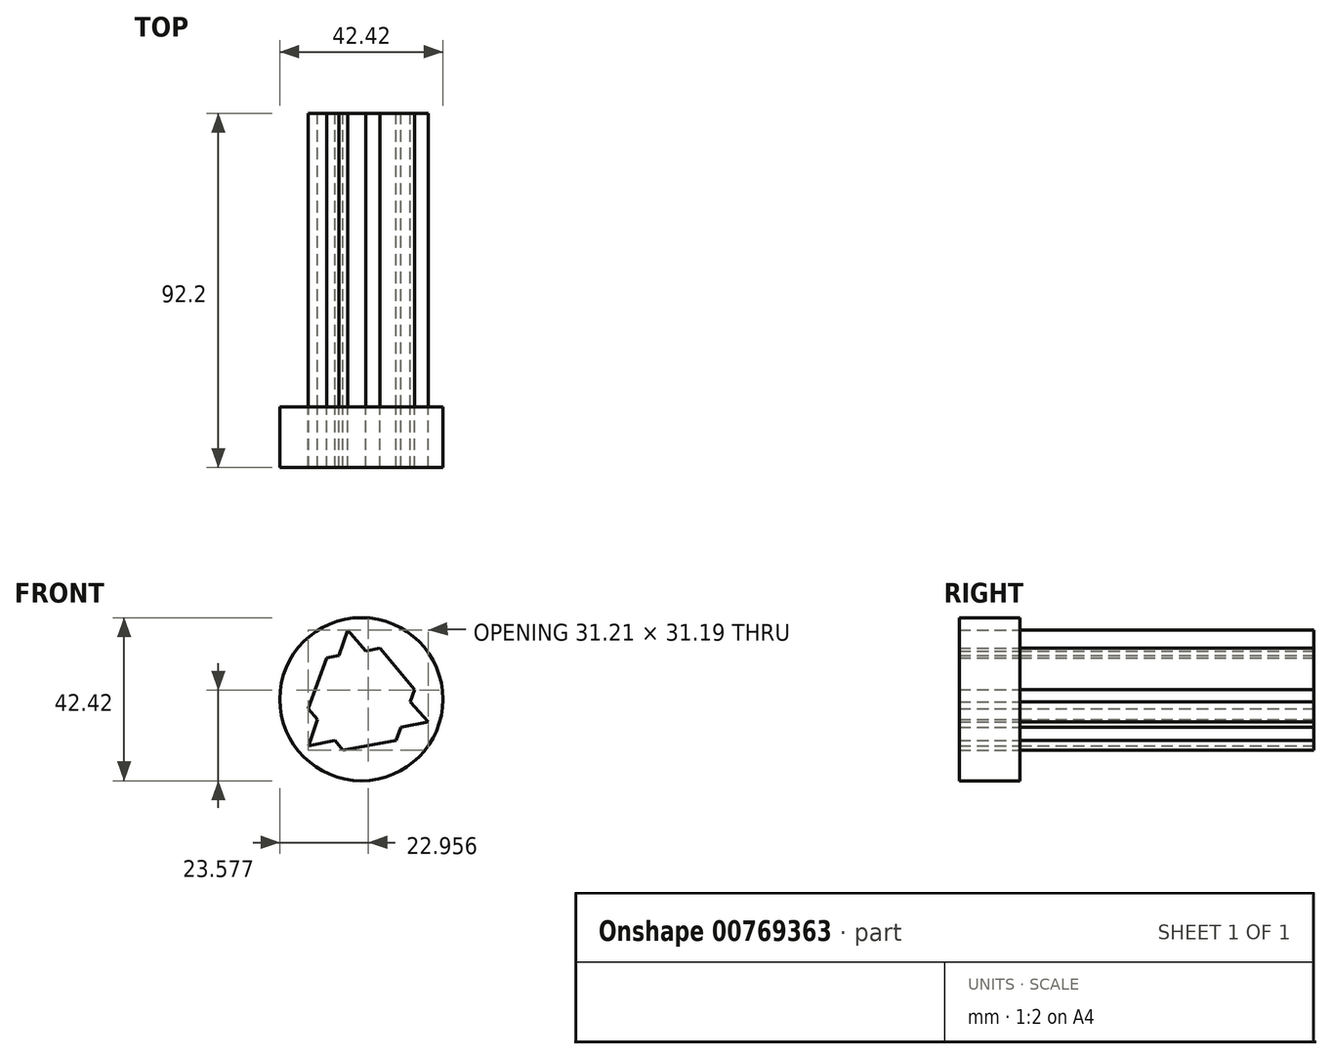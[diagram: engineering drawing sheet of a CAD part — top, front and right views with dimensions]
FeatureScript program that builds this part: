
annotation { "Feature Type Name" : "Feature", "Feature Type Description" : "" }
export const myFeature = defineFeature(function(context is Context, id is Id, definition is map)
    precondition{}
    {
        {
            var Q0;
            Q0=qCreatedBy(makeId("Front.planeOp"),FACE);
            var sketch = newSketch(context, id + "F0", { "sketchPlane" : qUnion([Q0])});
            skCircle(sketch, "E0.cCircle", {"center": v(0, 0) * mm, "radius": 14.08 * mm, "construction": true});
            skLineSegment(sketch, "E0.0", {"start": v(-9.05, 10.78) * mm, "end": v(4.8, 13.23) * mm});
            skLineSegment(sketch, "E0.1", {"start": v(4.8, 13.23) * mm, "end": v(13.86, 2.45) * mm});
            skLineSegment(sketch, "E0.2", {"start": v(13.86, 2.45) * mm, "end": v(9.05, -10.78) * mm});
            skLineSegment(sketch, "E0.3", {"start": v(9.05, -10.78) * mm, "end": v(-4.8, -13.23) * mm});
            skLineSegment(sketch, "E0.4", {"start": v(-4.8, -13.23) * mm, "end": v(-13.86, -2.45) * mm});
            skLineSegment(sketch, "E0.5", {"start": v(-13.86, -2.45) * mm, "end": v(-9.05, 10.78) * mm});
            skCircle(sketch, "E1.cCircle", {"center": v(0, 0) * mm, "radius": 18.32 * mm, "construction": true});
            skLineSegment(sketch, "E1.0", {"start": v(-3.6, 17.96) * mm, "end": v(17.35, -5.87) * mm});
            skLineSegment(sketch, "E1.1", {"start": v(17.35, -5.87) * mm, "end": v(-13.76, -12.1) * mm});
            skLineSegment(sketch, "E1.2", {"start": v(-13.76, -12.1) * mm, "end": v(-3.6, 17.96) * mm});
            skSolve(sketch);
        }
        {
            var Q0;
            {var subQ0=sQuery(id+"F0.wireOp",EDGE,"E0.1");Q0=makeQuery(id+"F0.imprint","IMPRINT",FACE,{"disambiguationData":[TD([[makeQuery(id+"F0.imprint","IMPRINT",EDGE,{"derivedFrom":subQ0}),-1.0]])]});}
            var Q1;
            {var subQ0=sQuery(id+"F0.wireOp",EDGE,"E0.5");Q1=makeQuery(id+"F0.imprint","IMPRINT",FACE,{"disambiguationData":[TD([[makeQuery(id+"F0.imprint","IMPRINT",EDGE,{"derivedFrom":subQ0}),-1.0]])]});}
            var Q2;
            {var subQ1=sQuery(id+"F0.wireOp",EDGE,"E0.0");var subQ8=sQuery(id+"F0.wireOp",EDGE,"E1.2");var subQ11=makeQuery(id+"F0.imprint","INTERSECT",VERTEX,{"derivedFrom":[subQ1,subQ8]});Q2=makeQuery(id+"F0.imprint","IMPRINT",FACE,{"disambiguationData":[TD([[makeQuery(id+"F0.imprint","IMPRINT",EDGE,{"disambiguationData":[TD([[subQ11,-1.0]])],"derivedFrom":subQ1}),-1.0]])]});}
            var Q3;
            {var subQ0=sQuery(id+"F0.wireOp",EDGE,"E0.3");Q3=makeQuery(id+"F0.imprint","IMPRINT",FACE,{"disambiguationData":[TD([[makeQuery(id+"F0.imprint","IMPRINT",EDGE,{"derivedFrom":subQ0}),-1.0]])]});}
            var Q4;
            {var subQ0=sQuery(id+"F0.wireOp",EDGE,"E1.2");var subQ1=sQuery(id+"F0.wireOp",EDGE,"E0.0");var subQ2=makeQuery(id+"F0.imprint","INTERSECT",VERTEX,{"derivedFrom":[subQ1,subQ0]});Q4=makeQuery(id+"F0.imprint","IMPRINT",FACE,{"disambiguationData":[TD([[makeQuery(id+"F0.imprint","IMPRINT",EDGE,{"disambiguationData":[TD([[subQ2,-1.0]])],"derivedFrom":subQ1}),1.0]])]});}
            var Q5;
            {var subQ0=sQuery(id+"F0.wireOp",EDGE,"E1.0");var subQ1=sQuery(id+"F0.wireOp",EDGE,"E0.2");var subQ2=makeQuery(id+"F0.imprint","INTERSECT",VERTEX,{"derivedFrom":[subQ1,subQ0]});Q5=makeQuery(id+"F0.imprint","IMPRINT",FACE,{"disambiguationData":[TD([[makeQuery(id+"F0.imprint","IMPRINT",EDGE,{"disambiguationData":[TD([[subQ2,-1.0]])],"derivedFrom":subQ1}),1.0]])]});}
            var Q6;
            {var subQ0=sQuery(id+"F0.wireOp",EDGE,"E1.1");var subQ1=sQuery(id+"F0.wireOp",EDGE,"E0.4");var subQ2=makeQuery(id+"F0.imprint","INTERSECT",VERTEX,{"derivedFrom":[subQ1,subQ0]});Q6=makeQuery(id+"F0.imprint","IMPRINT",FACE,{"disambiguationData":[TD([[makeQuery(id+"F0.imprint","IMPRINT",EDGE,{"disambiguationData":[TD([[subQ2,-1.0]])],"derivedFrom":subQ1}),1.0]])]});}
            extrude(context, id + "F1", {"entities" : qUnion([Q0, Q1, Q2, Q3, Q4, Q5, Q6]), "depth" : 76.4 * mm, "offsetDistance" : 25 * mm});
        }
        {
            var Q0;
            Q0=makeQuery(id+"F1.opExtrude","CAP_FACE",FACE,{"disambiguationData":[OSD([sQuery(id+"F0.wireOp",EDGE,"E0.0"),sQuery(id+"F0.wireOp",EDGE,"E0.1"),sQuery(id+"F0.wireOp",EDGE,"E0.2"),sQuery(id+"F0.wireOp",EDGE,"E0.3"),sQuery(id+"F0.wireOp",EDGE,"E0.4"),sQuery(id+"F0.wireOp",EDGE,"E0.5"),sQuery(id+"F0.wireOp",EDGE,"E1.0"),sQuery(id+"F0.wireOp",EDGE,"E1.1"),sQuery(id+"F0.wireOp",EDGE,"E1.2")])],"isStart":false});
            var sketch = newSketch(context, id + "F2", { "sketchPlane" : qUnion([Q0])});
            skCircle(sketch, "E2", {"center": v(0, 0) * mm, "radius": 21.21 * mm});
            skSolve(sketch);
        }
        {
            var Q0;
            Q0=makeQuery(id+"F2.imprint","IMPRINT",FACE,{"disambiguationData":[TD([[makeQuery(id+"F2.imprint","IMPRINT",EDGE,{"derivedFrom":sQuery(id+"F2.wireOp",EDGE,"E2")}),1.0]])]});
            extrude(context, id + "F3", {"entities" : qUnion([Q0]), "operationType" : NewBodyOperationType.ADD, "depth" : 15.8 * mm, "offsetDistance" : 25 * mm});
        }
    });
